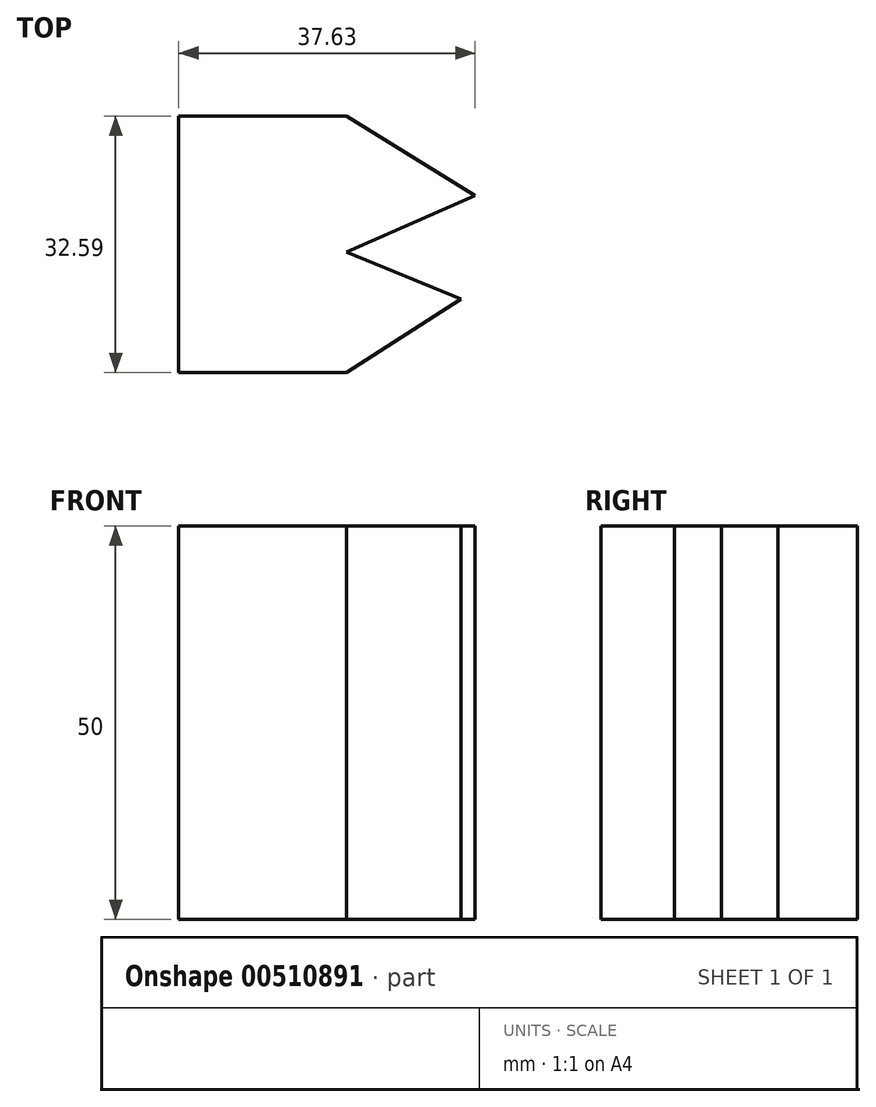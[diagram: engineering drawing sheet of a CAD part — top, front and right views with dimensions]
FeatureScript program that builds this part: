
annotation { "Feature Type Name" : "Feature", "Feature Type Description" : "" }
export const myFeature = defineFeature(function(context is Context, id is Id, definition is map)
    precondition{}
    {
        {
            var Q0;
            Q0=qCreatedBy(makeId("Top.planeOp"),FACE);
            var sketch = newSketch(context, id + "F0", { "sketchPlane" : qUnion([Q0])});
            skLineSegment(sketch, "E0", {"start": v(0, 23.28) * mm, "end": v(-21.34, 23.28) * mm});
            skLineSegment(sketch, "E1", {"start": v(-21.34, 23.28) * mm, "end": v(-21.34, -9.31) * mm});
            skLineSegment(sketch, "E2", {"start": v(-21.34, -9.31) * mm, "end": v(0, -9.31) * mm});
            skLineSegment(sketch, "E3", {"start": v(0, -9.31) * mm, "end": v(14.55, 0) * mm});
            skLineSegment(sketch, "E4", {"start": v(14.55, 0) * mm, "end": v(0, 6.01) * mm});
            skLineSegment(sketch, "E5", {"start": v(0, 6.01) * mm, "end": v(16.3, 13.19) * mm});
            skLineSegment(sketch, "E6", {"start": v(16.3, 13.19) * mm, "end": v(0, 23.28) * mm});
            skSolve(sketch);
        }
        {
            var Q0;
            Q0 = qSketchRegion(id + "F0", true);
            extrude(context, id + "F1", {"entities" : qUnion([Q0]), "depth" : 50 * mm});
        }
    });
